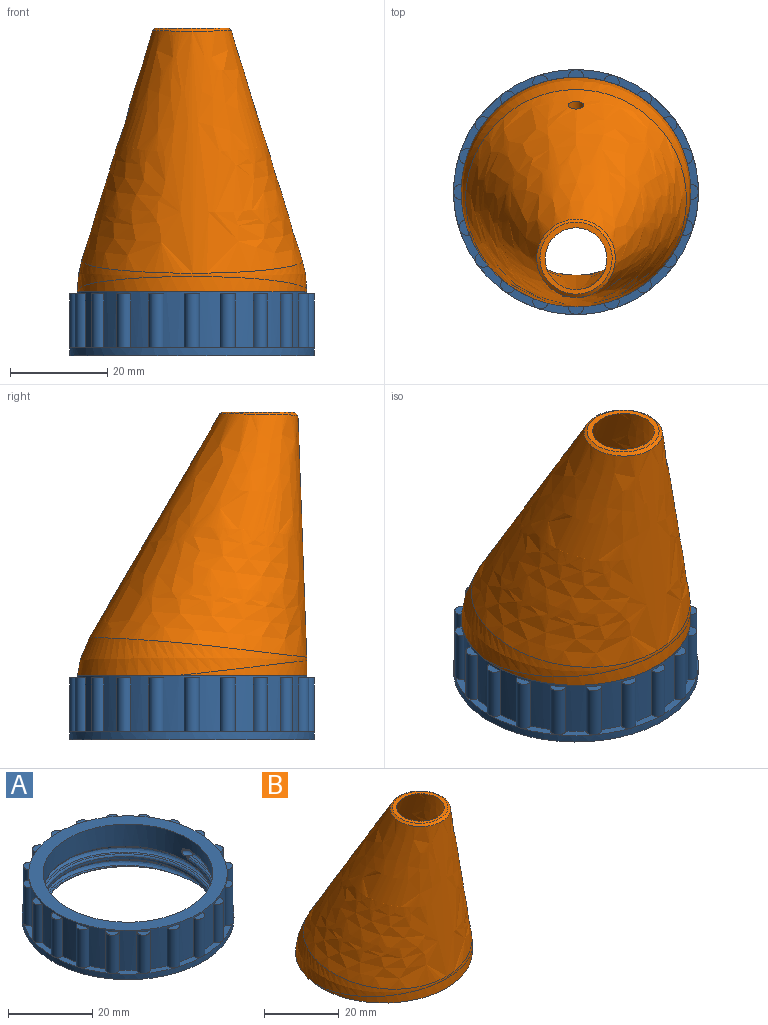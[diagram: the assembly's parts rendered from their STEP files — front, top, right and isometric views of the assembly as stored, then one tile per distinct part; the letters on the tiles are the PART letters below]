
ASSEMBLY  parts=2 mates=1
PART A: 85 faces, bbox 50.9x50.9x14.7 mm
  f0: plane 47.24x47.24mm, normal (0,0,1), area 472mm2, adj f1,f22
  f1: cylinder r=23.62mm len=47.24mm, axis (0,0,-1), area 1015.2mm2, adj f0,f2,f3,f4,f5,f6,f7,f8
  f2: plane 7.03x3.98mm, normal (0,0,1), area 8.2mm2, adj f1,f43,f62,f63
  f3: plane 7.79x2.3mm, normal (0,0,1), area 8.2mm2, adj f1,f43,f44,f63
  f4: plane 5.58x5.58mm, normal (0,0,1), area 8.2mm2, adj f1,f43,f61,f62
  f5: plane 7.03x3.98mm, normal (0,0,1), area 8.2mm2, adj f1,f43,f60,f61
  f6: plane 7.79x2.3mm, normal (0,0,1), area 8.2mm2, adj f1,f43,f59,f60
  f7: plane 7.79x2.3mm, normal (0,0,1), area 8.2mm2, adj f1,f43,f58,f59
  f8: plane 7.03x3.98mm, normal (0,0,1), area 8.2mm2, adj f1,f43,f57,f58
  f9: plane 5.58x5.58mm, normal (0,0,1), area 8.2mm2, adj f1,f43,f56,f57
  f10: plane 7.03x3.98mm, normal (0,0,1), area 8.2mm2, adj f1,f43,f55,f56
  f11: plane 7.79x2.3mm, normal (0,0,1), area 8.2mm2, adj f1,f43,f54,f55
  f12: plane 7.79x2.3mm, normal (0,0,1), area 8.2mm2, adj f1,f43,f53,f54
  f13: plane 7.03x3.98mm, normal (0,0,1), area 8.2mm2, adj f1,f43,f52,f53
  f14: plane 5.58x5.58mm, normal (0,0,1), area 8.2mm2, adj f1,f43,f51,f52
  f15: plane 7.03x3.98mm, normal (0,0,1), area 8.2mm2, adj f1,f43,f50,f51
  f16: plane 7.79x2.3mm, normal (0,0,1), area 8.2mm2, adj f1,f43,f49,f50
  f17: plane 7.79x2.3mm, normal (0,0,1), area 8.2mm2, adj f1,f43,f48,f49
  f18: plane 7.03x3.98mm, normal (0,0,1), area 8.2mm2, adj f1,f43,f47,f48
  f19: plane 5.58x5.58mm, normal (0,0,1), area 8.2mm2, adj f1,f43,f46,f47
  f20: plane 7.03x3.98mm, normal (0,0,1), area 8.2mm2, adj f1,f43,f45,f46
  f21: plane 7.79x2.3mm, normal (0,0,1), area 8.2mm2, adj f1,f43,f44,f45
  f22: cylinder r=20.19mm len=40.39mm, axis (0,0,-1), area 678.1mm2, adj f0,f23,f31,f35,f36,f37,f38,f39
  f23: cylinder r=20.19mm len=40.39mm, axis (0,0,-1), area 84.7mm2, adj f22,f31,f32,f35,f64
  f24: plane 50.95x50.95mm, normal (0,0,-1), area 516.7mm2, adj f26,f27,f28,f29,f43,f64
  f25: bspline ~42.57x42.57mm, area 148mm2, adj f26,f31,f41,f64
  f26: bspline ~44.3x44.3mm, area 393.8mm2, adj f24,f25,f27,f40,f64
  f27: cylinder r=22.15mm len=44.3mm, axis (0,0,-1), area 76.1mm2, adj f24,f26,f28,f33,f39
  f28: cylinder r=22.15mm len=4.46mm, axis (0,0,-1), area 0.3mm2, adj f24,f27,f29
  f29: bspline ~27.87x22.15mm, area 29.2mm2, adj f24,f28,f30,f33,f64
  f30: bspline ~21.28x21.28mm, area 12.9mm2, adj f29,f32,f34,f64
  f31: bspline ~41.37x41.37mm, area 167.2mm2, adj f22,f23,f25,f42,f64
  f32: bspline ~12.19x4.37mm, area 5.4mm2, adj f23,f30,f35,f64
  f33: bspline ~44.3x44.3mm, area 423.7mm2, adj f27,f29,f34,f38
  f34: bspline ~42.57x42.57mm, area 177.5mm2, adj f30,f33,f35,f37
  f35: bspline ~41.37x41.37mm, area 225.9mm2, adj f22,f23,f32,f34,f36
  f36: torus R=0.51mm, axis (0,0,-1), area 0.2mm2, adj f22,f35,f37
  f37: cone r=0.49mm half-angle=88.4deg, axis (0,0,-1), area 0.8mm2, adj f22,f34,f36,f38
  f38: torus R=1.07mm, axis (0,0,-1), area 3.6mm2, adj f22,f33,f37,f39
  f39: cylinder r=1.96mm len=2.05mm, axis (0,0,-1), area 0.8mm2, adj f22,f27,f38,f40
  f40: torus R=1.07mm, axis (0,0,-1), area 3.6mm2, adj f22,f26,f39,f41
  f41: cone r=1.09mm half-angle=88.4deg, axis (0,0,1), area 0.8mm2, adj f22,f25,f40,f42
  f42: torus R=0.51mm, axis (0,0,-1), area 0.2mm2, adj f22,f31,f41
  f43: cylinder r=25.21mm len=50.42mm, axis (0,0,-1), area 251.5mm2, adj f2,f3,f4,f5,f6,f7,f8,f9
  f44: cylinder r=1.59mm len=11.11mm, axis (0,0,-1), area 56.6mm2, adj f1,f3,f21,f84
  f45: cylinder r=1.59mm len=11.11mm, axis (0,0,-1), area 56.6mm2, adj f1,f20,f21,f83
  f46: cylinder r=1.59mm len=11.11mm, axis (0,0,-1), area 56.6mm2, adj f1,f19,f20,f82
  f47: cylinder r=1.59mm len=11.11mm, axis (0,0,-1), area 56.6mm2, adj f1,f18,f19,f81
  f48: cylinder r=1.59mm len=11.11mm, axis (0,0,-1), area 56.6mm2, adj f1,f17,f18,f80
  f49: cylinder r=1.59mm len=11.11mm, axis (0,0,-1), area 56.6mm2, adj f1,f16,f17,f79
  f50: cylinder r=1.59mm len=11.11mm, axis (0,0,-1), area 56.6mm2, adj f1,f15,f16,f78
  f51: cylinder r=1.59mm len=11.11mm, axis (0,0,-1), area 56.6mm2, adj f1,f14,f15,f77
  f52: cylinder r=1.59mm len=11.11mm, axis (0,0,-1), area 56.6mm2, adj f1,f13,f14,f76
  f53: cylinder r=1.59mm len=11.11mm, axis (0,0,-1), area 56.6mm2, adj f1,f12,f13,f75
  f54: cylinder r=1.59mm len=11.11mm, axis (0,0,-1), area 56.6mm2, adj f1,f11,f12,f74
  f55: cylinder r=1.59mm len=11.11mm, axis (0,0,-1), area 56.6mm2, adj f1,f10,f11,f73
  f56: cylinder r=1.59mm len=11.11mm, axis (0,0,-1), area 56.6mm2, adj f1,f9,f10,f72
  f57: cylinder r=1.59mm len=11.11mm, axis (0,0,-1), area 56.6mm2, adj f1,f8,f9,f71
  f58: cylinder r=1.59mm len=11.11mm, axis (0,0,-1), area 56.6mm2, adj f1,f7,f8,f70
  f59: cylinder r=1.59mm len=11.11mm, axis (0,0,-1), area 56.6mm2, adj f1,f6,f7,f69
  f60: cylinder r=1.59mm len=11.11mm, axis (0,0,-1), area 56.6mm2, adj f1,f5,f6,f68
  f61: cylinder r=1.59mm len=11.11mm, axis (0,0,-1), area 56.6mm2, adj f1,f4,f5,f67
  f62: cylinder r=1.59mm len=11.11mm, axis (0,0,-1), area 56.6mm2, adj f1,f2,f4,f66
  f63: cylinder r=1.59mm len=11.11mm, axis (0,0,-1), area 56.6mm2, adj f1,f2,f3,f65
  f64: cone r=20.19mm half-angle=45deg, axis (0,0,-1), area 93.4mm2, adj f23,f24,f25,f26,f29,f30,f31,f32
  f65: plane 3.11x2.13mm, normal (0,0,1), area 4mm2, adj f1,f63
  f66: plane 2.9x2.56mm, normal (0,0,1), area 4mm2, adj f1,f62
  f67: plane 2.9x2.56mm, normal (0,0,1), area 4mm2, adj f1,f61
  f68: plane 3.11x2.13mm, normal (0,0,1), area 4mm2, adj f1,f60
  f69: plane 3.18x1.64mm, normal (0,0,1), area 4mm2, adj f1,f59
  f70: plane 3.11x2.13mm, normal (0,0,1), area 4mm2, adj f1,f58
  f71: plane 2.9x2.56mm, normal (0,0,1), area 4mm2, adj f1,f57
  f72: plane 2.9x2.56mm, normal (0,0,1), area 4mm2, adj f1,f56
  f73: plane 3.11x2.13mm, normal (0,0,1), area 4mm2, adj f1,f55
  f74: plane 3.18x1.64mm, normal (0,0,1), area 4mm2, adj f1,f54
  f75: plane 3.11x2.13mm, normal (0,0,1), area 4mm2, adj f1,f53
  f76: plane 2.9x2.56mm, normal (0,0,1), area 4mm2, adj f1,f52
  f77: plane 2.9x2.56mm, normal (0,0,1), area 4mm2, adj f1,f51
  f78: plane 3.11x2.13mm, normal (0,0,1), area 4mm2, adj f1,f50
  f79: plane 3.18x1.64mm, normal (0,0,1), area 4mm2, adj f1,f49
  f80: plane 3.11x2.13mm, normal (0,0,1), area 4mm2, adj f1,f48
  f81: plane 2.9x2.56mm, normal (0,0,1), area 4mm2, adj f1,f47
  f82: plane 2.9x2.56mm, normal (0,0,1), area 4mm2, adj f1,f46
  f83: plane 3.11x2.13mm, normal (0,0,1), area 4mm2, adj f1,f45
  f84: plane 3.18x1.64mm, normal (0,0,1), area 4mm2, adj f1,f44
PART B: 8 faces, bbox 47.5x47.3x56 mm
  f0: plane 14.94x14.9mm, normal (0,0,1), area 47.4mm2, adj f1,f4
  f1: bspline ~54.23x37.34mm, area 4133mm2, adj f0,f2,f3
  f2: plane 47.25x47.17mm, normal (0,0,-1), area 826.9mm2, adj f1,f6,f7
  f3: cylinder r=1.59mm len=7.09mm, axis (0,-0.86,-0.5), area 61.8mm2, adj f1,f5
  f4: bspline ~16.15x16.07mm, area 38.9mm2, adj f0,f5
  f5: bspline ~49.82x47.02mm, area 4891.8mm2, adj f3,f4,f6
  f6: bspline ~47.38x47.25mm, area 759.2mm2, adj f2,f5,f7
  f7: cylinder r=23.62mm len=47.24mm, axis (0,0,-1), area 122.8mm2, adj f2,f6
PLACE A t=(0,0,-13.18)mm
PLACE B t=(0,0,-17.78)mm
MATE fastened B.f7 <-> A.f1  axis (0,0,1) through (0,0,0)mm
